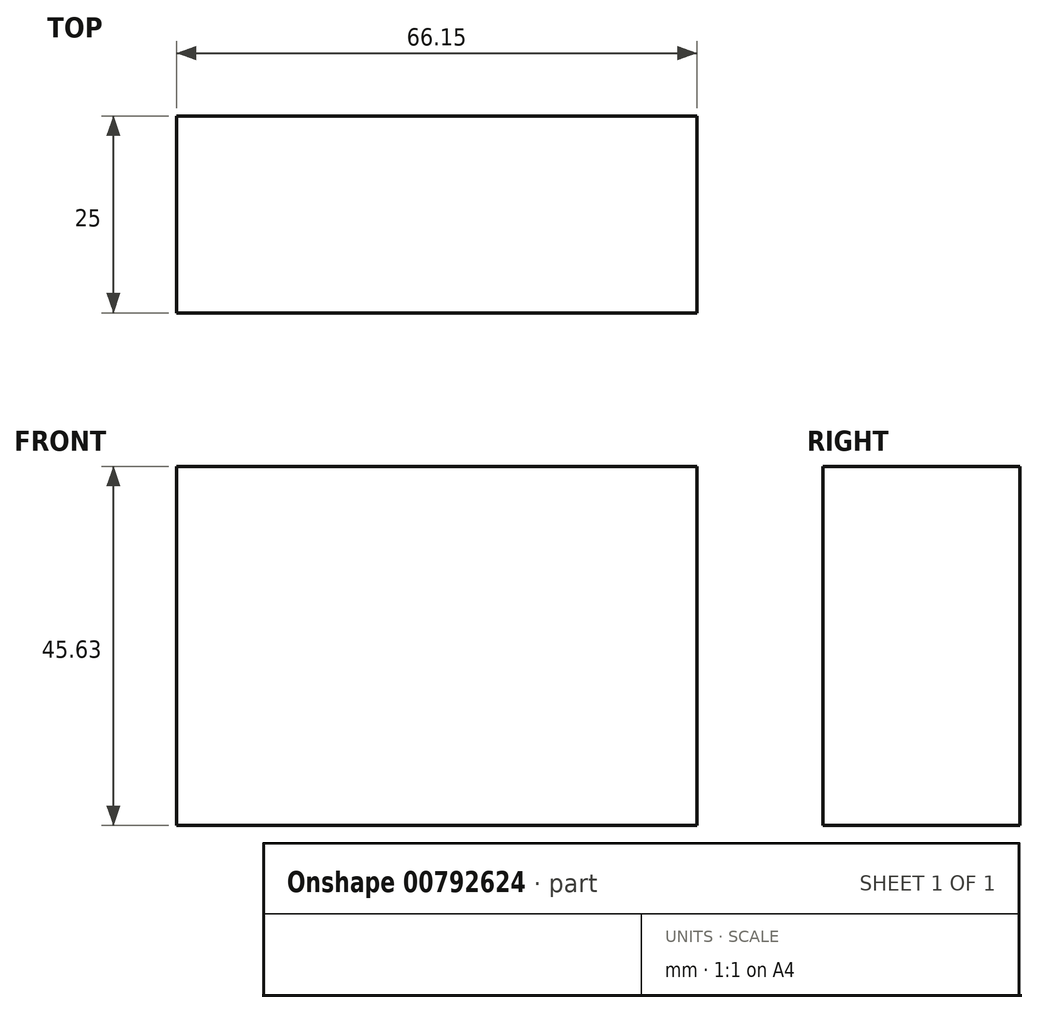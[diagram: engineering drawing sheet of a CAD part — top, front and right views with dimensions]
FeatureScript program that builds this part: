
annotation { "Feature Type Name" : "Feature", "Feature Type Description" : "" }
export const myFeature = defineFeature(function(context is Context, id is Id, definition is map)
    precondition{}
    {
        {
            var Q0;
            Q0=qCreatedBy(makeId("Front.planeOp"),FACE);
            var sketch = newSketch(context, id + "F0", { "sketchPlane" : qUnion([Q0])});
            skLineSegment(sketch, "E0.bottom", {"start": v(-127.6, 29.17) * mm, "end": v(-61.45, 29.17) * mm});
            skLineSegment(sketch, "E0.top", {"start": v(-127.6, -16.46) * mm, "end": v(-61.45, -16.46) * mm});
            skLineSegment(sketch, "E0.left", {"start": v(-127.6, 29.17) * mm, "end": v(-127.6, -16.46) * mm});
            skLineSegment(sketch, "E0.right", {"start": v(-61.45, 29.17) * mm, "end": v(-61.45, -16.46) * mm});
            skSolve(sketch);
        }
        {
            var Q0;
            Q0 = qSketchRegion(id + "F0", true);
            extrude(context, id + "F1", {"entities" : qUnion([Q0]), "depth" : 25 * mm, "offsetDistance" : 25 * mm});
        }
    });
